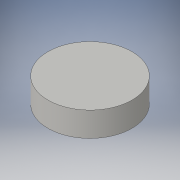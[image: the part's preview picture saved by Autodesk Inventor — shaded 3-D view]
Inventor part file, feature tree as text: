
AUTODESK INVENTOR PART (.ipt)
format: ipt  version: 2016 (Build 200138000, 138)  size: 87,552 bytes
history: native  units: in
note: dims shown in document units (in); Inventor stores cm internally (conversion verified against a paired STEP export)
features: extrude x1, sketch x1
ambient origin geometry x8: Origin, YZ Plane, XZ Plane, XY Plane, X Axis, Y Axis, Z Axis, Center Point
bodies: Solid1 (feature_tree)
feature tree (2):
  extrude  "Extrusion1"  Depth=0.9843in TaperAngle=0.0deg
  sketch  "Sketch1"  dims[d0=3.374in d1=0.9843in d2=0.0in]
